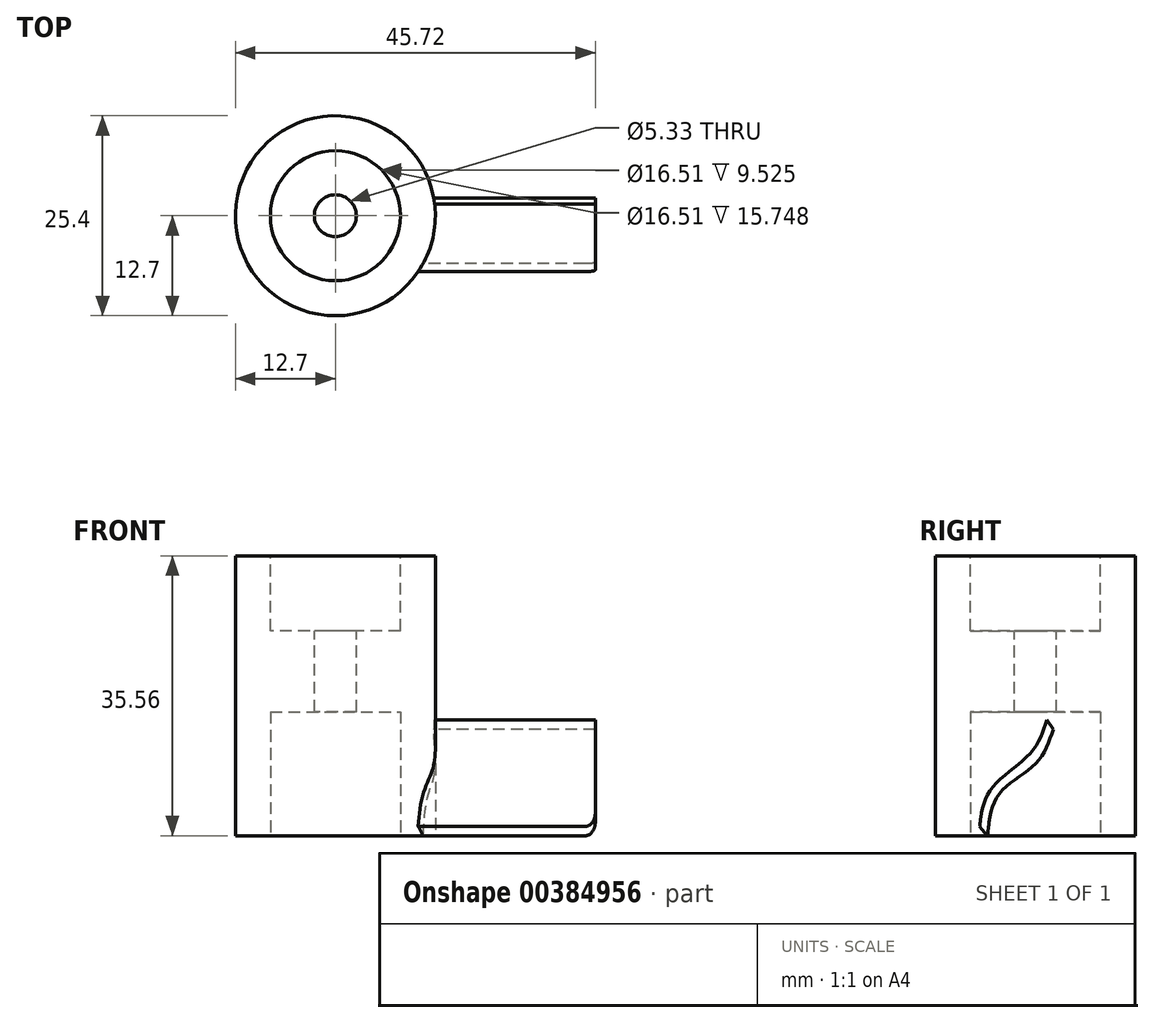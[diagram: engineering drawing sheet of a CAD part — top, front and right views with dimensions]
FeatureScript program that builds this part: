
annotation { "Feature Type Name" : "Feature", "Feature Type Description" : "" }
export const myFeature = defineFeature(function(context is Context, id is Id, definition is map)
    precondition{}
    {
        {
            var Q0;
            Q0=qCreatedBy(makeId("Top.planeOp"),FACE);
            var sketch = newSketch(context, id + "F0", { "sketchPlane" : qUnion([Q0])});
            skCircle(sketch, "E0", {"center": v(0, 0) * mm, "radius": 12.7 * mm});
            skSolve(sketch);
        }
        {
            var Q0;
            Q0 = qSketchRegion(id + "F0", true);
            extrude(context, id + "F1", {"entities" : qUnion([Q0]), "depth" : 35.56 * mm});
        }
        {
            var Q0;
            Q0=makeQuery(id+"F1.opExtrude","CAP_FACE",FACE,{"disambiguationData":[OSD([sQuery(id+"F0.wireOp",EDGE,"E0")])],"isStart":false});
            var sketch = newSketch(context, id + "F2", { "sketchPlane" : qUnion([Q0])});
            skCircle(sketch, "E1", {"center": v(0, 0) * mm, "radius": 8.26 * mm});
            skSolve(sketch);
        }
        {
            var Q0;
            Q0 = qSketchRegion(id + "F2", true);
            extrude(context, id + "F3", {"entities" : qUnion([Q0]), "operationType" : NewBodyOperationType.REMOVE, "oppositeDirection" : true, "depth" : 9.52 * mm});
        }
        {
            var Q0;
            Q0=makeQuery(id+"F3.boolean.opBoolean","COPY",FACE,{"derivedFrom":makeQuery(id+"F3.opExtrude","CAP_FACE",FACE,{"disambiguationData":[OSD([sQuery(id+"F2.wireOp",EDGE,"E1")])],"isStart":false})});
            var sketch = newSketch(context, id + "F4", { "sketchPlane" : qUnion([Q0])});
            skCircle(sketch, "E2", {"center": v(0, 0) * mm, "radius": 2.67 * mm});
            skSolve(sketch);
        }
        {
            var Q0;
            Q0 = qSketchRegion(id + "F4", true);
            extrude(context, id + "F5", {"entities" : qUnion([Q0]), "operationType" : NewBodyOperationType.REMOVE, "oppositeDirection" : true, "depth" : 254 * mm});
        }
        {
            var Q0;
            Q0=makeQuery(id+"F1.opExtrude","CAP_FACE",FACE,{"disambiguationData":[OSD([sQuery(id+"F0.wireOp",EDGE,"E0")])],"isStart":true});
            var sketch = newSketch(context, id + "F6", { "sketchPlane" : qUnion([Q0])});
            skCircle(sketch, "E3", {"center": v(0, 0) * mm, "radius": 8.26 * mm});
            skSolve(sketch);
        }
        {
            var Q0;
            Q0=qCreatedBy(makeId("Right.planeOp"),FACE);
            cPlane(context, id + "F7", {"entities" : qUnion([Q0]), "cplaneType" : CPlaneType.OFFSET, "offset" : 7.62 * mm, "width" : 152.4 * mm, "height" : 152.4 * mm});
        }
        {
            var Q0;
            Q0=qCreatedBy(id+"F7.planeOp",FACE);
            var sketch = newSketch(context, id + "F8", { "sketchPlane" : qUnion([Q0])});
            skLineSegment(sketch, "E4", {"start": v(-6.1, 0) * mm, "end": v(-7.1, 1.18) * mm});
            skFitSpline(sketch, "E5", {"points": [v(-7.1, 1.18) * mm, v(-5.67, 5.91) * mm, v(-0.7, 10.46) * mm, v(1.47, 14.71) * mm], "startDerivative": vector(1.84, 15.66) * mm, "endDerivative": vector(4.74, 14.16) * mm});
            skFitSpline(sketch, "E6", {"points": [v(-6.1, 0) * mm, v(-4.59, 5.34) * mm, v(0, 9.16) * mm, v(2.26, 13.49) * mm], "startDerivative": vector(1.8, 17.37) * mm, "endDerivative": vector(5.1, 14.74) * mm});
            skLineSegment(sketch, "E7", {"start": v(1.47, 14.71) * mm, "end": v(2.26, 13.49) * mm});
            skSolve(sketch);
        }
        {
            var Q0;
            Q0 = qSketchRegion(id + "F8", true);
            extrude(context, id + "F9", {"entities" : qUnion([Q0]), "operationType" : NewBodyOperationType.ADD, "depth" : 25.4 * mm});
        }
        {
            var Q0;
            Q0=makeQuery(id+"F9.opExtrude","CAP_EDGE",EDGE,{"disambiguationData":[OSD([sQuery(id+"F8.wireOp",EDGE,"E4")])],"isStart":false});
            var Q1;
            Q1=makeQuery(id+"F9.opExtrude","CAP_EDGE",EDGE,{"disambiguationData":[OSD([sQuery(id+"F8.wireOp",EDGE,"qyySMabw-nsSV-lFSh-00nw-PXK11i2kIjkb")])],"isStart":false});
            fillet(context, id + "F10", {"entities" : qUnion([Q0, Q1]), "radius" : 1.27 * mm, "tangentPropagation" : true, "allowEdgeOverflow" : false});
        }
        {
            var Q0;
            Q0=makeQuery(id+"F6.imprint","IMPRINT",FACE,{"disambiguationData":[TD([[makeQuery(id+"F6.imprint","IMPRINT",EDGE,{"derivedFrom":sQuery(id+"F6.wireOp",EDGE,"E3")}),1.0]])]});
            extrude(context, id + "F11", {"entities" : qUnion([Q0]), "operationType" : NewBodyOperationType.REMOVE, "oppositeDirection" : true, "depth" : 15.75 * mm});
        }
    });
